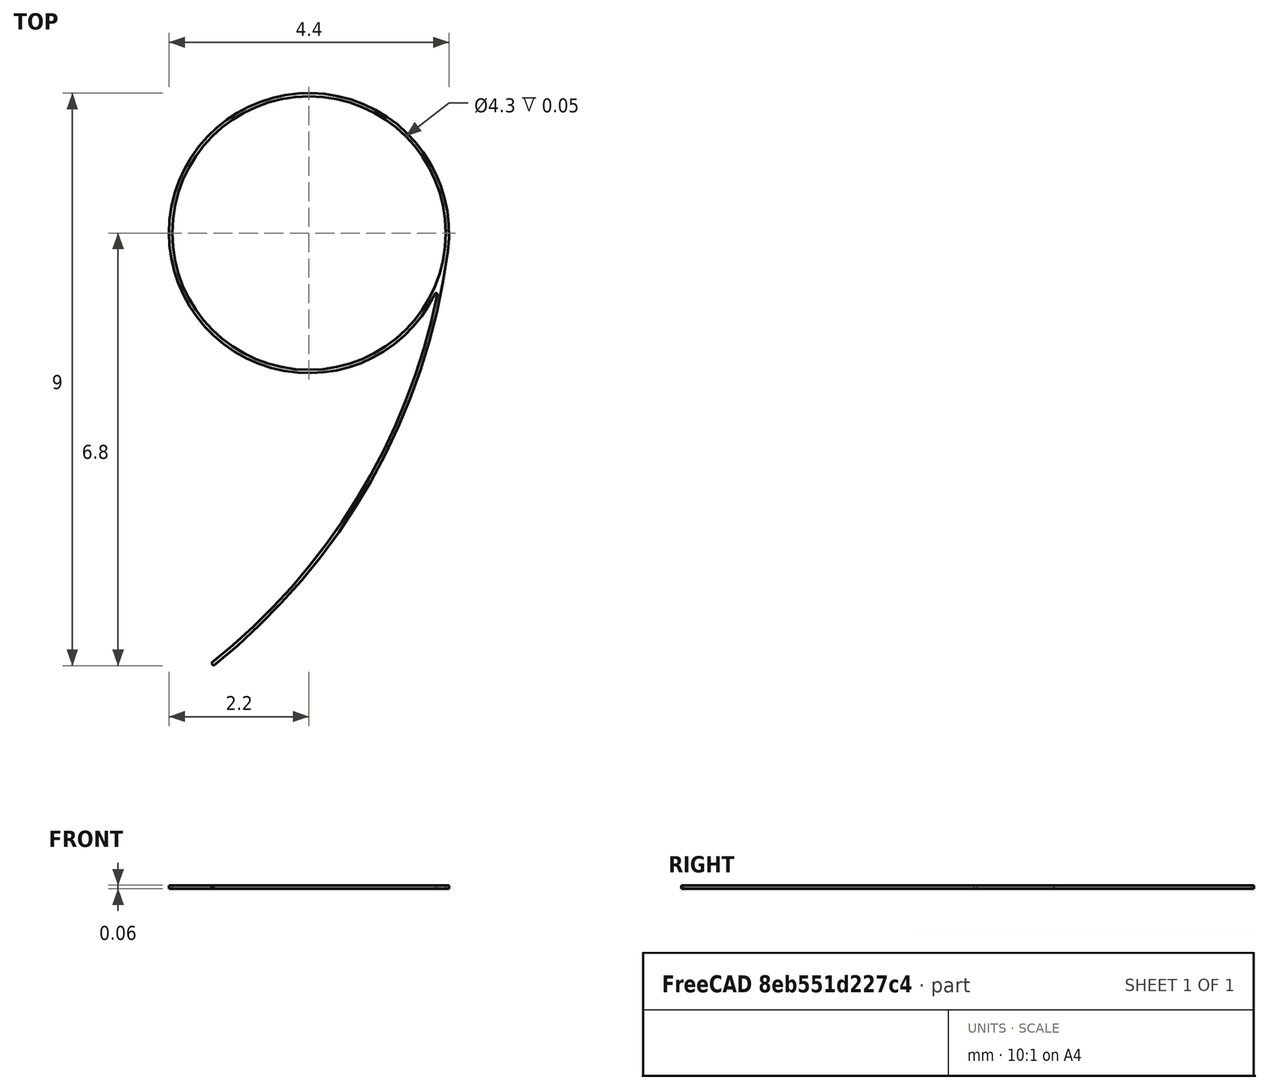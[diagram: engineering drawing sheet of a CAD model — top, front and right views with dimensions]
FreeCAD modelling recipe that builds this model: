
FCSTD DOCUMENT  (FreeCAD 0.16R6712 (Git))
Label: 9t
License: All rights reserved
LicenseURL: http://en.wikipedia.org/wiki/All_rights_reserved
objects: Sketcher::SketchObject×1, PartDesign::Pad×1, Mesh::Feature×1
note: 3 computed .brp shape members not serialized (recipe doc carries the construction recipe); baked Part::Feature solids carry a one-line shape summary decoded from their .brp

FEATURE [Sketcher::SketchObject] Sketch
  sketch-geometry (6):
    g0: ArcOfCircle CenterX=-7.73305 CenterY=7.81979 CenterZ=0 NormalX=0 NormalY=0 NormalZ=1 Radius=10 StartAngle=5.38535 EndAngle=6.1521
    g1: ArcOfCircle CenterX=-7.73305 CenterY=7.81979 CenterZ=0 NormalX=0 NormalY=0 NormalZ=1 Radius=9.95 StartAngle=5.38535 EndAngle=6.08207
    g2: LineSegment StartX=-1.53117 StartY=0.0390989 StartZ=0 EndX=-1.5 EndY=0 EndZ=0
    g3: ArcOfCircle CenterX=1.9968 CenterY=5.83613 CenterZ=0 NormalX=0 NormalY=0 NormalZ=1 Radius=0.02 StartAngle=6.08208 EndAngle=8.44826
    g4: ArcOfCircle CenterX=0 CenterY=6.8 CenterZ=0 NormalX=0 NormalY=0 NormalZ=1 Radius=2.2 StartAngle=6.15223 EndAngle=12.1212
    g5: Circle CenterX=0 CenterY=6.8 CenterZ=0 NormalX=0 NormalY=0 NormalZ=1 Radius=2.15
  constraints (20):
    c: PointOnObject(g0,g-1)
    c: Radius(g0) = 10
    c: Coincident(g1,g0)
    c: Radius(g1) = 9.95
    c: Coincident(g2,g0)
    c: PointOnObject(g1,g2)
    c: Perpendicular(g1,g2,g1) = 4.71239
    c: Coincident(g1,g2)
    c: DistanceX(g-2,g0) = -1.5
    c: PointOnObject(g3,g1)
    c: Tangent(g3,g1)
    c: Coincident(g3,g1)
    c: PointOnObject(g4,g-2)
    c: Coincident(g4,g3)
    c: Coincident(g4,g0)
    c: Radius(g4) = 2.2
    c: Coincident(g5,g4)
    c: Radius(g5) = 2.15
    c: DistanceY(g-1,g4) = 6.8
    c: Radius(g3) = 0.02
FEATURE [PartDesign::Pad] Pad
  Length = 0.05
  Length2 = 100
  Midplane = true
  Sketch = -> Sketch
  Type = 0
FEATURE [Mesh::Feature] Mesh  label="Pad (Meshed)"
